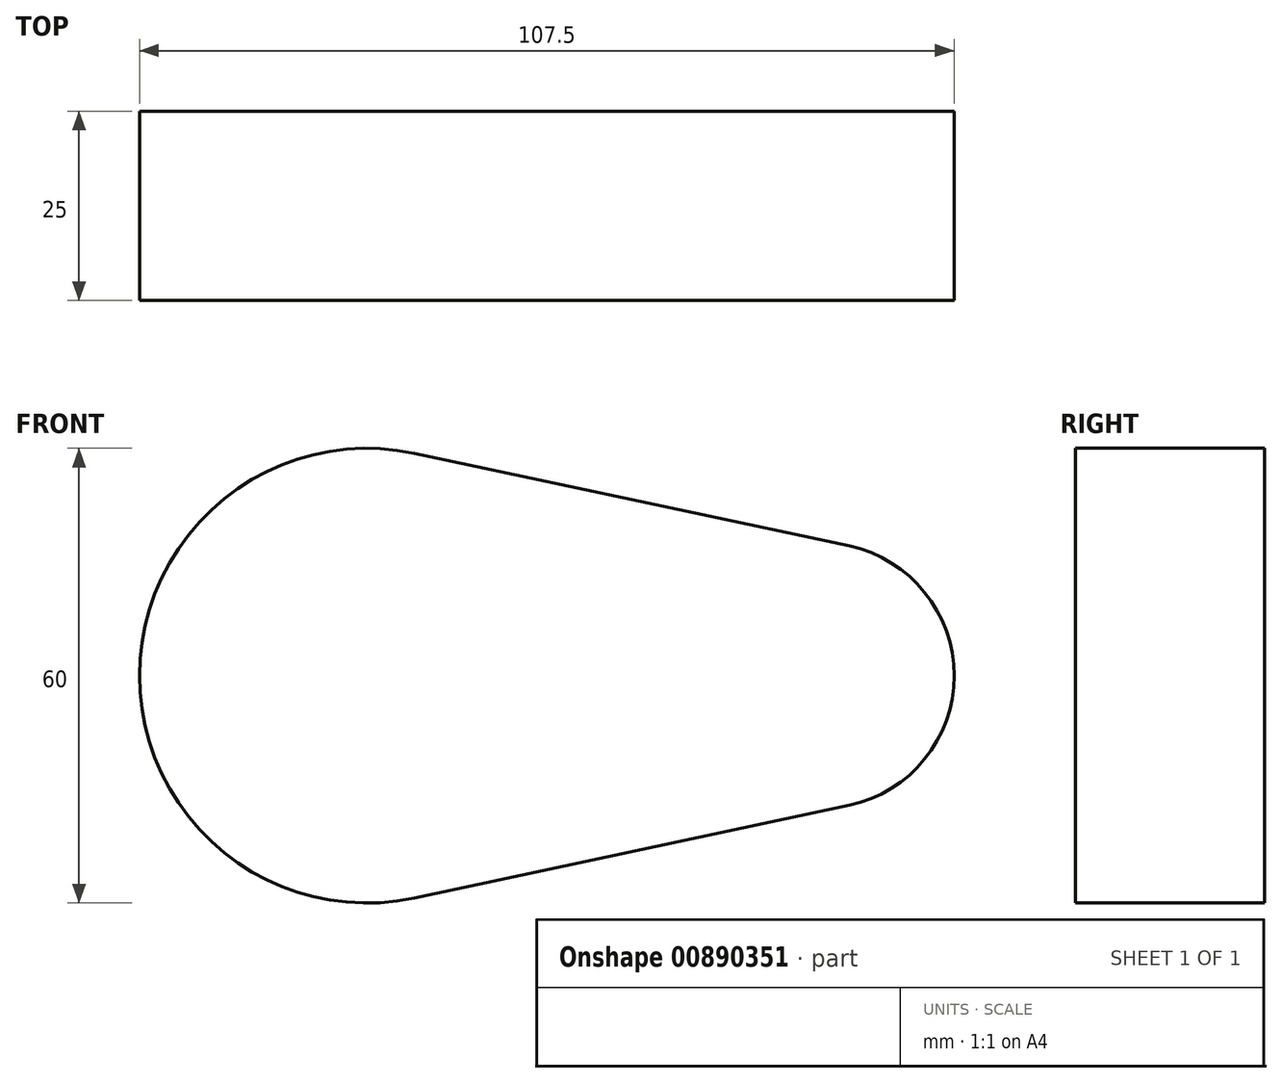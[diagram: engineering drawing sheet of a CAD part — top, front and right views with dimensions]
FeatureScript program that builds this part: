
annotation { "Feature Type Name" : "Feature", "Feature Type Description" : "" }
export const myFeature = defineFeature(function(context is Context, id is Id, definition is map)
    precondition{}
    {
        {
            var Q0;
            Q0=qCreatedBy(makeId("Front.planeOp"),FACE);
            var sketch = newSketch(context, id + "F0", { "sketchPlane" : qUnion([Q0])});
            skCircle(sketch, "E0", {"center": v(0, 0) * mm, "radius": 30 * mm});
            skCircle(sketch, "E1", {"center": v(60, 0) * mm, "radius": 17.5 * mm});
            skLineSegment(sketch, "E2", {"start": v(6.25, 29.34) * mm, "end": v(63.65, 17.12) * mm});
            skLineSegment(sketch, "E3", {"start": v(6.25, -29.34) * mm, "end": v(63.65, -17.12) * mm});
            skSolve(sketch);
        }
        {
            var Q0;
            {var subQ0=sQuery(id+"F0.wireOp",EDGE,"E0");var subQ1=makeQuery(id+"F0.imprint","INTERSECT",VERTEX,{"derivedFrom":[subQ0,sQuery(id+"F0.wireOp",EDGE,"E2")]});Q0=makeQuery(id+"F0.imprint","IMPRINT",FACE,{"disambiguationData":[TD([[makeQuery(id+"F0.imprint","IMPRINT",EDGE,{"disambiguationData":[TD([[subQ1,-1.0]])],"derivedFrom":subQ0}),1.0]])]});}
            var Q1;
            {var subQ0=sQuery(id+"F0.wireOp",EDGE,"E2");Q1=makeQuery(id+"F0.imprint","IMPRINT",FACE,{"disambiguationData":[TD([[makeQuery(id+"F0.imprint","IMPRINT",EDGE,{"derivedFrom":subQ0}),-1.0]])]});}
            var Q2;
            {var subQ0=sQuery(id+"F0.wireOp",EDGE,"E1");var subQ1=makeQuery(id+"F0.imprint","INTERSECT",VERTEX,{"derivedFrom":[subQ0,sQuery(id+"F0.wireOp",EDGE,"E2")]});Q2=makeQuery(id+"F0.imprint","IMPRINT",FACE,{"disambiguationData":[TD([[makeQuery(id+"F0.imprint","IMPRINT",EDGE,{"disambiguationData":[TD([[subQ1,-1.0]])],"derivedFrom":subQ0}),1.0]])]});}
            extrude(context, id + "F1", {"entities" : qUnion([Q0, Q1, Q2]), "depth" : 25 * mm, "offsetDistance" : 25 * mm});
        }
    });
